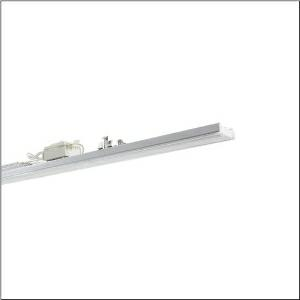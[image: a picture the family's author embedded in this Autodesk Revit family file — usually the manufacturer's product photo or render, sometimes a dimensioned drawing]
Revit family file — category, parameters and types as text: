
# Revit family: licross_r__21_recessed_ho_52tl1wcn4c5m_df97
name_source: partatom
category: Lighting Fixtures
units: mm (PartAtom-declared; Revit-internal decimal feet)

## family parameters
Cut with Voids When Loaded = No
Host = Face
Light Source = No
Part Type = Normal
Room Calculation Point = No
Round Connector Dimension = Use Diameter
Shared = No

## types (1)
- --- (1 x LED, 12710 lm, 68.4 W, 4000K)
    Apparent Load = 68 VA
    CIE Flux Codes = 73 94 99 100 100
    Color Rendering = 80
    Color Temperature = 4000K
    Default Elevation = 1800 mm
    Description = Licross® 21 Recessed HO, luminaire insert, of sheet steel, galvanised, coil coated, white, length: 1.500mm, width: 66mm, height: 67mm, LED rated luminous flux: 12.710lm, light colour: 840, control gear: ON/OFF Multilumen, CLOi, control gear: ECG Multilumen, with plug, 3-pole, with phase selection, mains connection: 220..240V, AC, 50/60Hz, start of lifetime: 68W, end of service life: 83W, internal wiring halogen-free, primary optical cover: cover, of PMMA, light emission: direct distribution, primary light characteristic: symmetric, protection rating (complete): IP40, insulation class (complete): insulation class I (protective earthing), certification: CE, ENEC, VDE, UKCA, protection symbol: D if used in an environment without relevant dust loads with corresponding accessories, impact resistance: IK06, permissible ambient temperature for indoor applications: -35..+30°C, corresponds to IFS (International Featured Standards) requirements for safety and quality in the food industry, reducing of maximum allowable ambient temperature of 5°C with ceiling mounting, LABS conformity tested according to VDMA 24364:2018-05, packaging unit: 1 piece
    Height = 58 mm
    Lamp = 1 x LED
    Lamp Light Flux = 12710 lm
    Lamp Power = 68.4 W
    Lamp count = 1
    Length = 1500 mm
    Luminous efficacy = 186 lm/W
    Manufacturer = Siteco
    ModVariant = No
    Model = 52TL1WCN4C5M
    Mounting Place = Ceiling
    Mounting Type = Pendant
    Number of Poles = 1
    OnlyDefault = Yes
    Power Factor = 1
    Product Name = Licross® 21 Recessed HO
    Product group = luminaire insert | ceiling pendant
    ProductGroupID = 902
    Protection Class = Protection class I
    Protection Degree = IP 40
    RLX_Detail_Level = 1
    RLX_Emergency_Light_Flux = 0 lm
    RLX_Emergency_Type = 0
    RLX_Emergency_Type_DB = No
    RlxData = <blob elided: 22365 chars, md5=768b390c>
    Socket = socket
    Standby Power = 0 W
    System Light Flux = 12710 lm
    System Power = 68 W
    Type Comments = factory setting: luminous flux: 100 % | (A | C | E) | 161 mA
    Type Image = l_1296930.jpg
    URL = http://relux.com
    VarID = @adj_080333
    Voltage = 0 V
    Weight = 0.00 kg
    Width = 66 mm

## geometry (parser evidence)
native form markers: Blend x4, Sweep x11
no freeform markers — native parametric forms only
